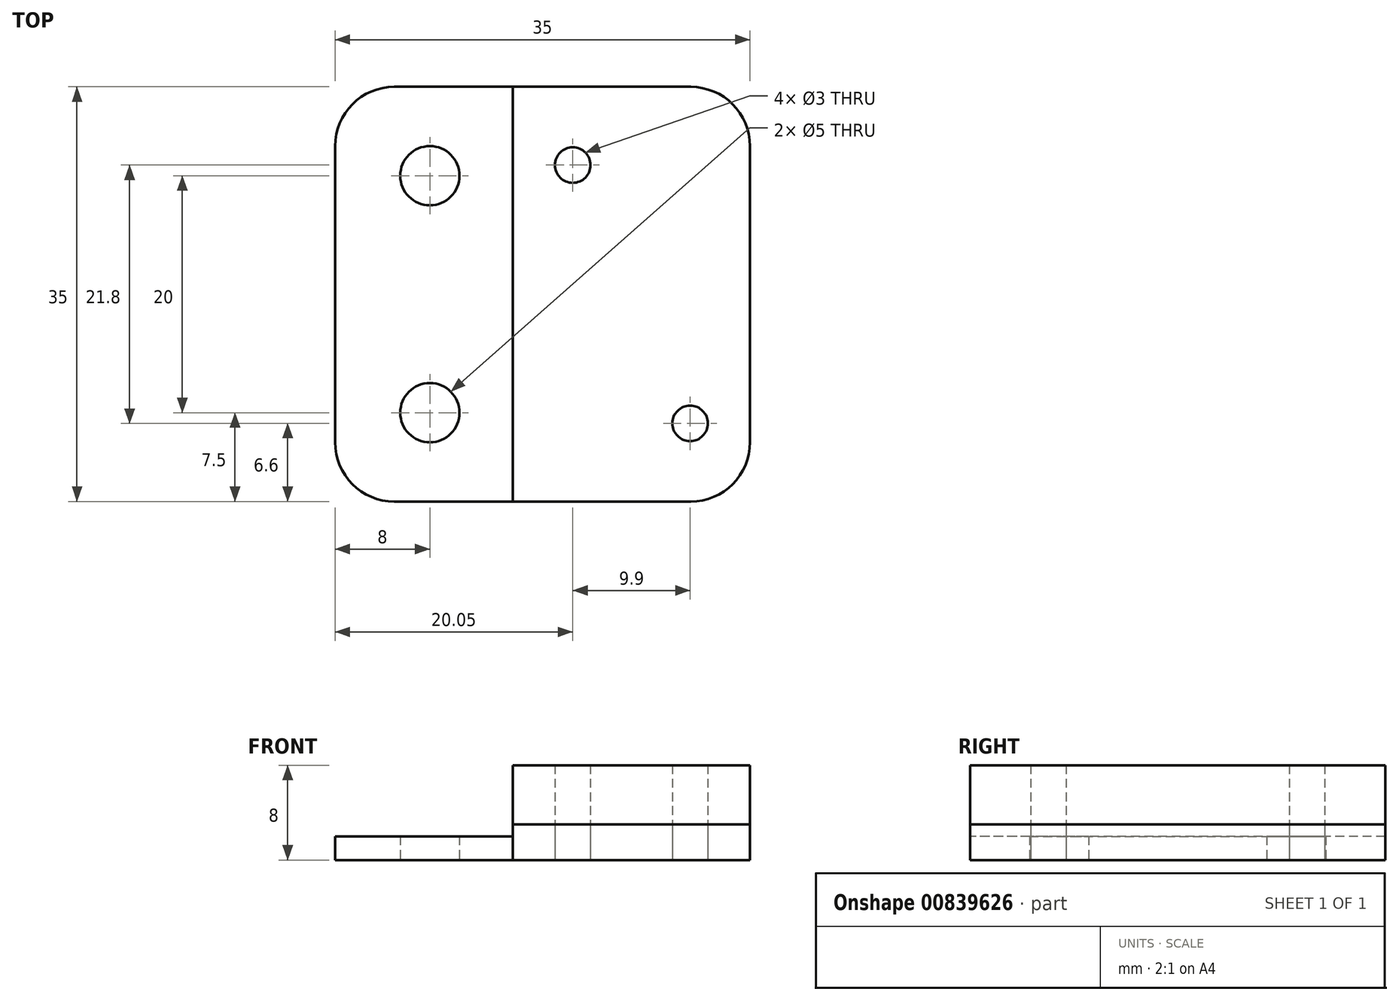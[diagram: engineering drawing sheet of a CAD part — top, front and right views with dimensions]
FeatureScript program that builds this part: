
annotation { "Feature Type Name" : "Feature", "Feature Type Description" : "" }
export const myFeature = defineFeature(function(context is Context, id is Id, definition is map)
    precondition{}
    {
        {
            var Q0;
            Q0=qCreatedBy(makeId("Top.planeOp"),FACE);
            var sketch = newSketch(context, id + "F0", { "sketchPlane" : qUnion([Q0])});
            skLineSegment(sketch, "E0.bottom", {"start": v(12.5, -17.5) * mm, "end": v(-12.5, -17.5) * mm});
            skLineSegment(sketch, "E0.top", {"start": v(12.5, 17.5) * mm, "end": v(-12.5, 17.5) * mm});
            skLineSegment(sketch, "E0.left", {"start": v(17.5, -12.5) * mm, "end": v(17.5, 12.5) * mm});
            skLineSegment(sketch, "E0.right", {"start": v(-17.5, -12.5) * mm, "end": v(-17.5, 12.5) * mm});
            skPoint(sketch, "E0.middle", {"position": v(0, 0) * mm});
            skLineSegment(sketch, "E1", {"start": v(-17.5, 0) * mm, "end": v(-9.5, 0) * mm, "construction": true});
            skLineSegment(sketch, "E2", {"start": v(-9.5, 0) * mm, "end": v(-9.5, 10) * mm, "construction": true});
            skCircle(sketch, "E3", {"center": v(-9.5, 10) * mm, "radius": 0.28 * mm});
            skCircle(sketch, "E4", {"center": v(-9.5, 10) * mm, "radius": 2.5 * mm});
            skCircle(sketch, "E5.MirrorC", {"center": v(-9.5, -10) * mm, "radius": 2.5 * mm});
            skPoint(sketch, "E6.visualSharp", {"position": v(-17.5, 17.5) * mm});
            skArc(sketch, "E6.filletArc", {"start": v(-12.5, 17.5) * mm, "mid": v(-16.04, 16.04) * mm, "end": v(-17.5, 12.5) * mm});
            skPoint(sketch, "E7.visualSharp", {"position": v(-17.5, -17.5) * mm});
            skArc(sketch, "E7.filletArc", {"start": v(-17.5, -12.5) * mm, "mid": v(-16.04, -16.04) * mm, "end": v(-12.5, -17.5) * mm});
            skPoint(sketch, "E8.visualSharp", {"position": v(17.5, 17.5) * mm});
            skArc(sketch, "E8.filletArc", {"start": v(17.5, 12.5) * mm, "mid": v(16.04, 16.04) * mm, "end": v(12.5, 17.5) * mm});
            skPoint(sketch, "E9.visualSharp", {"position": v(17.5, -17.5) * mm});
            skArc(sketch, "E9.filletArc", {"start": v(12.5, -17.5) * mm, "mid": v(16.04, -16.04) * mm, "end": v(17.5, -12.5) * mm});
            skLineSegment(sketch, "E10", {"start": v(17.5, 0) * mm, "end": v(-2.5, 0) * mm, "construction": true});
            skLineSegment(sketch, "E11", {"start": v(-2.5, 17.5) * mm, "end": v(-2.5, -17.5) * mm});
            skPoint(sketch, "E12", {"position": v(7.5, 0) * mm});
            skLineSegment(sketch, "E13.bottom", {"start": v(2.55, 10.9) * mm, "end": v(12.45, 10.9) * mm, "construction": true});
            skLineSegment(sketch, "E13.top", {"start": v(2.55, -10.9) * mm, "end": v(12.45, -10.9) * mm, "construction": true});
            skLineSegment(sketch, "E13.left", {"start": v(2.55, 10.9) * mm, "end": v(2.55, -10.9) * mm, "construction": true});
            skLineSegment(sketch, "E13.right", {"start": v(12.45, 10.9) * mm, "end": v(12.45, -10.9) * mm, "construction": true});
            skCircle(sketch, "E14", {"center": v(2.55, 10.9) * mm, "radius": 1.5 * mm});
            skCircle(sketch, "E15", {"center": v(12.45, -10.9) * mm, "radius": 1.5 * mm});
            skSolve(sketch);
        }
        {
            var Q0;
            Q0=makeQuery(id+"F0.imprint","IMPRINT",FACE,{"disambiguationData":[TD([[makeQuery(id+"F0.imprint","IMPRINT",EDGE,{"derivedFrom":sQuery(id+"F0.wireOp",EDGE,"E0.left")}),1.0]])]});
            extrude(context, id + "F1", {"entities" : qUnion([Q0]), "depth" : 3 * mm, "offsetDistance" : 25 * mm});
        }
        {
            var Q0;
            Q0=makeQuery(id+"F0.imprint","IMPRINT",FACE,{"disambiguationData":[TD([[makeQuery(id+"F0.imprint","IMPRINT",EDGE,{"derivedFrom":sQuery(id+"F0.wireOp",EDGE,"E0.right")}),-1.0]])]});
            extrude(context, id + "F2", {"entities" : qUnion([Q0]), "operationType" : NewBodyOperationType.ADD, "depth" : 2 * mm, "offsetDistance" : 25 * mm});
        }
        {
            var Q0;
            Q0=makeQuery(id+"F0.imprint","IMPRINT",FACE,{"disambiguationData":[TD([[makeQuery(id+"F0.imprint","IMPRINT",EDGE,{"derivedFrom":sQuery(id+"F0.wireOp",EDGE,"E0.left")}),1.0]])]});
            extrude(context, id + "F3", {"entities" : qUnion([Q0]), "depth" : 8 * mm, "offsetDistance" : 25 * mm});
        }
    });
